# Revit family: Sanitary_Showers_AXOR_12672XXX-AXOR-Starck-Shower-column-with-thermostat-and-overhead-shower-240-1jet
name_source: partatom
category: Plumbing Fixtures
revit_build: Autodesk Revit 2018 (Build: 20190510_1515(x64)
units: mm (PartAtom-declared; Revit-internal decimal feet)

## family parameters
Always vertical = No
Cut with Voids When Loaded = No
OmniClass Number = 23.31.17.00
OmniClass Title = Showers
Part Type = Normal
Room Calculation Point = No
Round Connector Dimension = Use Diameter
Shared = No
Work Plane-Based = Yes

## types (12) — shared parameters
Always visible = Yes
BIMobject category = Showers
Default Elevation = 1219.2 mm  [stored 4 ft]
Description = AXOR Starck Shower column with thermostat and overhead shower 240 1jet
Design country = Germany
EAN code = 4059625435182
Edition number = 1
GTIN code = https://4059625435182
IFC Classification = Sanitary Terminal
Manufacturer = AXOR
Manufacturer country = Germany
Manufacturer name = AXOR
Material main = Metal
Model = 12672XXX
OmniClass Code = 23-31 17 00
OmniClass Description = Showers
Product Guid = c7cc3b50-f89f-462c-9f16-0baaa737ee60
Product SKU = 12672XXX
Product data url = https://bimobject.com
Product family = AXOR Starck
Product group = Shower columns
Product name = 12672XXX AXOR Starck Shower column with thermostat and overhead shower 240 1jet
QR code = https://bimobject.com
URL = https://www.axor-design.com
Water Inlet = 12.7 mm  [stored 0.0416667 ft]
Water Inlet Description = Water Inlet DN15
Weight Net (Kg) = 14,2

## per-type parameters (varying)
| type | Material 1 |
| 800 Stainless Steel Optic | AXOR - Metal - 800 Stainless Steel Optic |
| 950 Brushed Brass | AXOR - Metal - 950 Brushed Brass |
| 310 Brushed Red Gold | AXOR - Metal - 310 Brushed Red Gold |
| 990 Polished Gold Optic | AXOR - Metal - 990 Polished Gold Optic |
| 300 Polished Red Gold | AXOR - Metal - 300 Polished Red Gold |
| 820 Brushed Nickel | AXOR - Metal - 820 Brushed Nickel |
| 330 Polished Black Chrome | AXOR - Metal - 330 Polished Black Chrome |
| 140 Brushed Bronze | AXOR - Metal - 140 Brushed Bronze |
| 250 Brushed Gold Optic | AXOR - Metal - 250 Brushed Gold Optic |
| 340 Brushed Black Chrome | AXOR - Metal - 340 Brushed Black Chrome |
| 000 Chrome | AXOR - Metal - 000 Chrome |
| 670 Matt Black | AXOR - Metal - 670 Matt Black |

note: [stored X ft] marks values corroborated as IEEE doubles in the binary element streams (Revit-internal decimal feet)

## geometry (parser evidence)
native form markers: Sweep x3
no freeform markers — native parametric forms only
